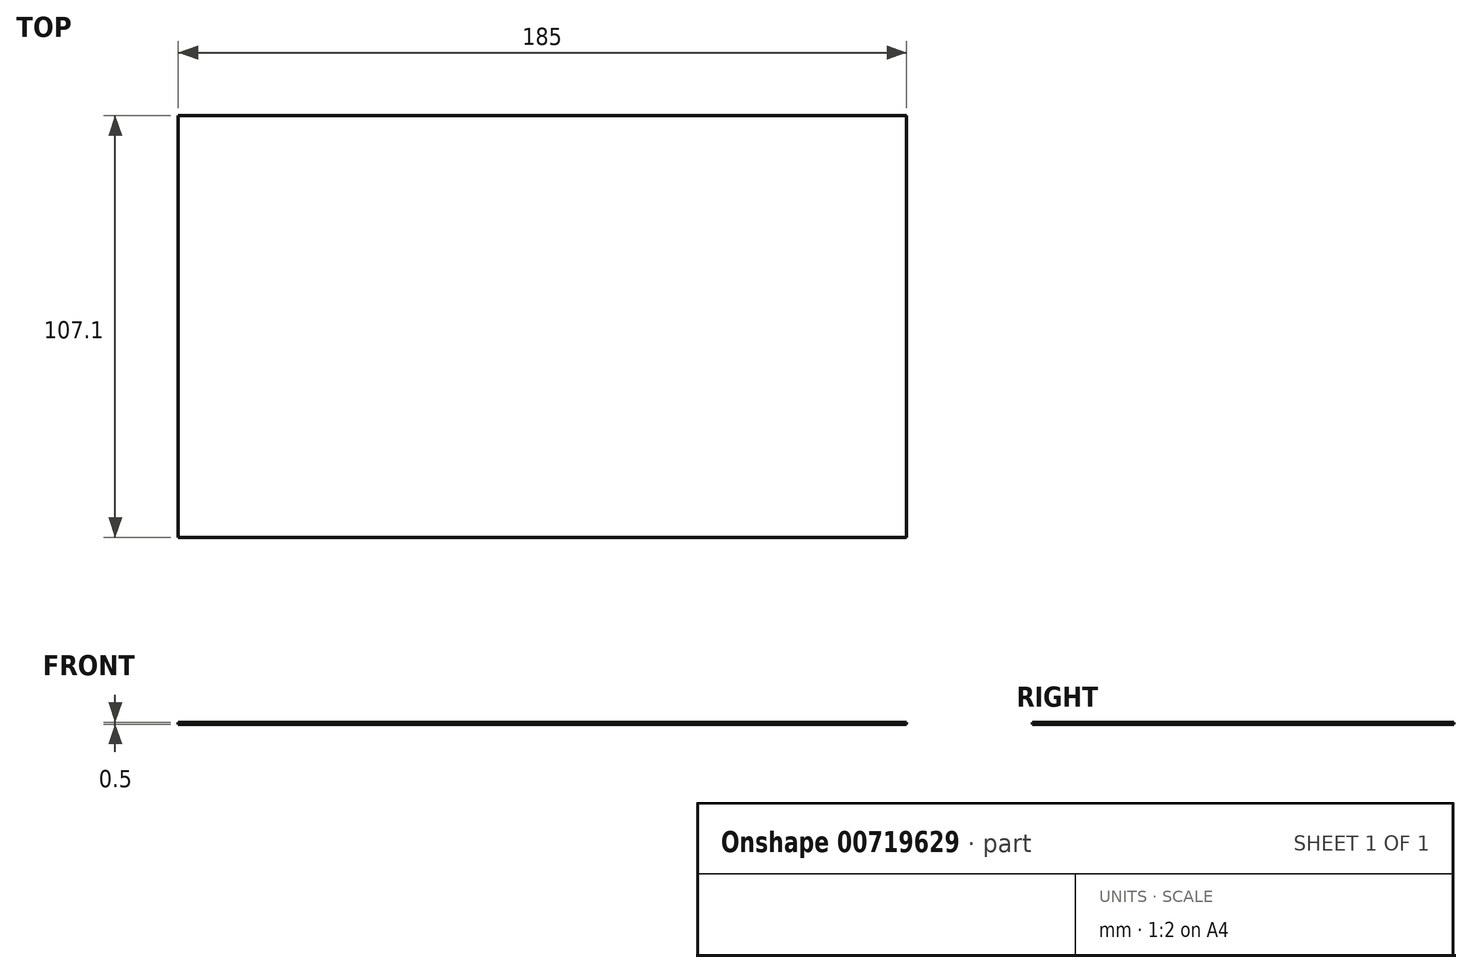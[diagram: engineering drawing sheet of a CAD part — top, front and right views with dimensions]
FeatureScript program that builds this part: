
annotation { "Feature Type Name" : "Feature", "Feature Type Description" : "" }
export const myFeature = defineFeature(function(context is Context, id is Id, definition is map)
    precondition{}
    {
        {
            var Q0;
            Q0=qCreatedBy(makeId("Front.planeOp"),FACE);
            var sketch = newSketch(context, id + "F0", { "sketchPlane" : qUnion([Q0])});
            skLineSegment(sketch, "E0.bottom", {"start": v(-20.75, 19.7) * mm, "end": v(164.25, 19.7) * mm});
            skLineSegment(sketch, "E0.top", {"start": v(-20.75, 19.2) * mm, "end": v(164.25, 19.2) * mm});
            skLineSegment(sketch, "E0.left", {"start": v(-20.75, 19.7) * mm, "end": v(-20.75, 19.2) * mm});
            skLineSegment(sketch, "E0.right", {"start": v(164.25, 19.7) * mm, "end": v(164.25, 19.2) * mm});
            skSolve(sketch);
        }
        {
            var Q0;
            Q0=makeQuery(id+"F0.imprint","IMPRINT",FACE,{"disambiguationData":[TD([[makeQuery(id+"F0.imprint","IMPRINT",EDGE,{"derivedFrom":sQuery(id+"F0.wireOp",EDGE,"E0.bottom")}),-1.0]])]});
            extrude(context, id + "F1", {"entities" : qUnion([Q0]), "depth" : 107.1 * mm});
        }
    });
